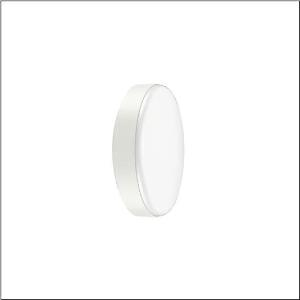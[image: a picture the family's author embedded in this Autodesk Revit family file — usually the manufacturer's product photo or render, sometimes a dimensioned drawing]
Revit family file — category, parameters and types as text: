
# Revit family: round_31_51wc10ma42as
name_source: partatom
category: Lighting Fixtures
units: mm (PartAtom-declared; Revit-internal decimal feet)

## family parameters
Cut with Voids When Loaded = No
Host = Face
Light Source = No
Part Type = Normal
Room Calculation Point = No
Round Connector Dimension = Use Diameter
Shared = No

## types (1)
- --- (1 x LED, 2550 lm, 20.5 W, 4000K)
    Apparent Load = 21 VA
    CIE Flux Codes = 44 75 94 94 100
    Color Rendering = 80
    Color Temperature = 4000K
    Default Elevation = 1800 mm
    Description = Round 31, wall and ceiling luminaire, primary optical cover: cover, of PC, opal, light emission: direct distribution, primary light characteristic: symmetric, installation type: surface-mounted, LED, rated luminous flux: 2.550lm, luminous efficacy: 124lm/W, light colour: 840, colour temperature: 4000K, control gear: ON/OFF Multilumen, with terminal, 3-pole, max. 2.5mm², mains connection: 220..240V, AC, 50/60Hz, rated input power: 20.5W, luminaire housing, of PC, traffic white (RAL 9016), diameter: 350mm, brightness and presence sensor, HF sensor, protection rating (complete): IP65, insulation class (complete): insulation class II (safety insulation), certification: CE, impact resistance: IK10, permissible operating ambient temperature: -20..+40°C, permissible storage temperature: -20..+60°C, packaging unit: 1 piece
    Height = 97 mm
    Lamp = 1 x LED
    Lamp Light Flux = 2550 lm
    Lamp Power = 20.5 W
    Lamp count = 1
    Length = 350 mm
    Luminous efficacy = 124 lm/W
    Manufacturer = Siteco
    ModVariant = No
    Model = 51WC10MA42AS
    Mounting Place = Wall
    Mounting Type = Surface mounted
    Number of Poles = 1
    OnlyDefault = Yes
    Power Factor = 1
    Product Name = Round 31
    Product group = wall and ceiling luminaire
    ProductGroupID = 2001
    Protection Class = Protection class II
    Protection Degree = IP 65
    RLX_Detail_Level = 1
    RLX_Emergency_Light_Flux = 0 lm
    RLX_Emergency_Type = 0
    RLX_Emergency_Type_DB = No
    RlxData = <blob elided: 30349 chars, md5=46c1c05e>
    Socket = socket
    Standby Power = 0 W
    System Light Flux = 2550 lm
    System Power = 21 W
    Type Comments = factory setting: luminous flux: 100 % | (ON | ON)
    Type Image = l_1007027.jpg
    URL = http://relux.com
    VarID = @adj_154091
    Voltage = 0 V
    Weight = 0.00 kg
    Width = 0 mm  [stored 0 ft]

note: [stored X ft] marks values corroborated as IEEE doubles in the binary element streams (Revit-internal decimal feet)

## geometry (parser evidence)
native form markers: Blend x4, Sweep x14
no freeform markers — native parametric forms only
